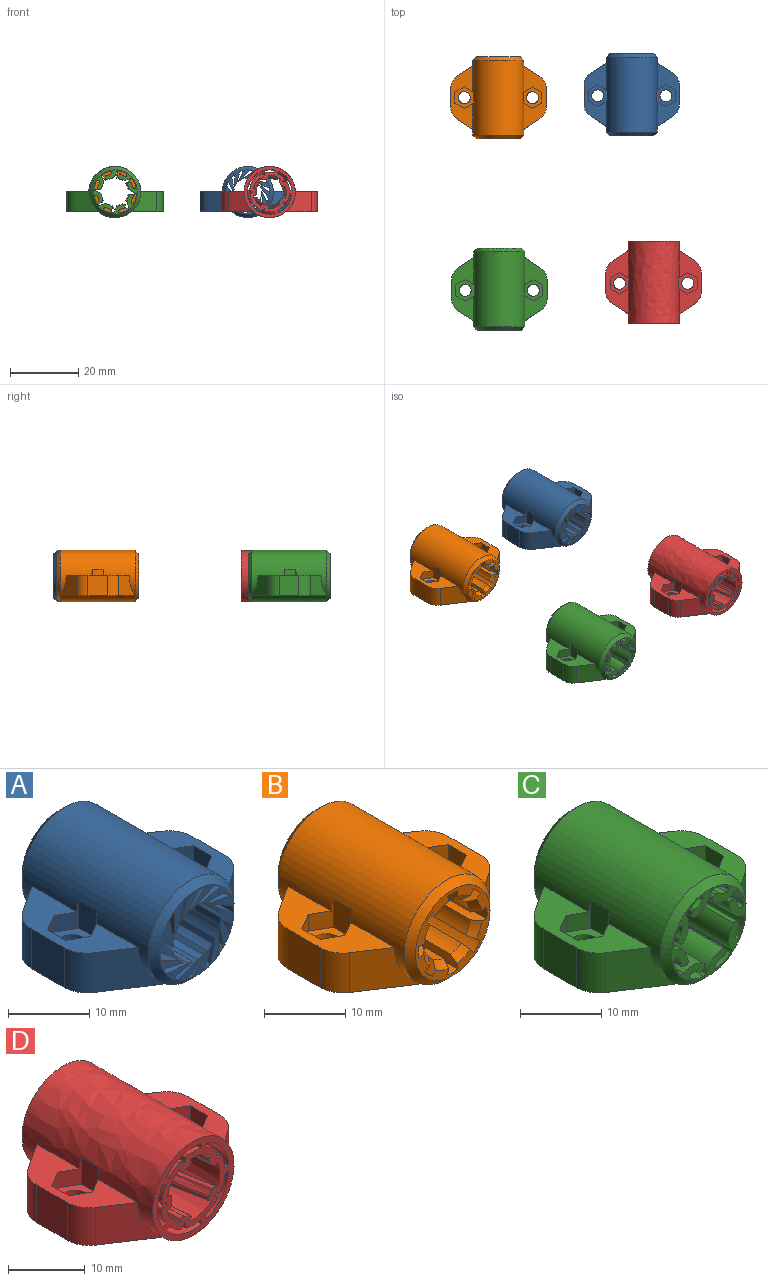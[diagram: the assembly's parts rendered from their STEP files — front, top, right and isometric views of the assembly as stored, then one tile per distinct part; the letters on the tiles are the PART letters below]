
ASSEMBLY  parts=4 mates=3
PART A: 96 faces, bbox 28x24x15 mm
  f0: plane 18.57x6.5mm, normal (0,0,1), area 66.1mm2, adj f1,f2,f6,f7,f8,f9,f87,f88
  f1: cylinder r=7.5mm len=22mm, axis (0,1,0), area 529.7mm2, adj f0,f6,f7,f69,f70,f71,f76,f77
  f2: plane 6x5.69mm, normal (-1,0,0), area 34.2mm2, adj f0,f3,f8,f9
  f3: plane 22x9.3mm, normal (0,0,-1), area 139mm2, adj f2,f4,f5,f6,f7,f8,f9,f10
  f4: plane 0.2x0.17mm, normal (0,-1,0), area 0mm2, adj f3,f6,f69
  f5: plane 0.2x0.17mm, normal (0,1,0), area 0mm2, adj f3,f7,f70
  f6: plane 7.3x6mm, normal (-0.55,-0.83,0), area 39.7mm2, adj f0,f1,f3,f4,f8
  f7: plane 7.3x6mm, normal (-0.55,0.83,0), area 39.7mm2, adj f0,f1,f3,f5,f9
  f8: cylinder r=4mm len=6mm, axis (0,0,-1), area 23.7mm2, adj f0,f2,f3,f6
  f9: cylinder r=4mm len=6mm, axis (0,0,-1), area 23.7mm2, adj f0,f2,f3,f7
  f10: cylinder r=7.5mm len=22mm, axis (0,1,0), area 223.5mm2, adj f3,f69,f70,f72
  f11: cylinder r=6.35mm len=24mm, axis (0,1,0), area 28.5mm2, adj f12,f66,f67,f68
  f12: plane 24x3.15mm, normal (-0.9,0,-0.44), area 84.3mm2, adj f11,f13,f67,f68
  f13: cylinder r=4.1mm len=24mm, axis (0,1,0), area 25.8mm2, adj f12,f14,f67,f68
  f14: plane 24x3.44mm, normal (0.98,0,0.2), area 84.3mm2, adj f13,f15,f67,f68
  f15: cylinder r=6.35mm len=24mm, axis (0,1,0), area 28.5mm2, adj f14,f16,f67,f68
  f16: plane 24x3.51mm, normal (-1,0,-0.01), area 84.3mm2, adj f15,f17,f67,f68
  f17: cylinder r=4.1mm len=24mm, axis (0,1,0), area 25.8mm2, adj f16,f18,f67,f68
  f18: plane 24x3.4mm, normal (0.97,0,-0.25), area 84.3mm2, adj f17,f19,f67,f68
  f19: cylinder r=6.35mm len=24mm, axis (0,1,0), area 28.5mm2, adj f18,f20,f67,f68
  f20: plane 24x3.18mm, normal (-0.91,0,0.42), area 84.3mm2, adj f19,f21,f67,f68
  f21: cylinder r=4.1mm len=24mm, axis (0,1,0), area 25.8mm2, adj f20,f22,f67,f68
  f22: plane 24x2.69mm, normal (0.77,0,-0.64), area 84.3mm2, adj f21,f23,f67,f68
  f23: cylinder r=6.35mm len=24mm, axis (0,1,0), area 28.5mm2, adj f22,f24,f67,f68
  f24: plane 24x2.72mm, normal (-0.63,0,0.77), area 84.3mm2, adj f23,f25,f67,f68
  f25: cylinder r=4.1mm len=24mm, axis (0,1,0), area 25.8mm2, adj f24,f26,f67,f68
  f26: plane 24x3.2mm, normal (0.41,0,-0.91), area 84.3mm2, adj f25,f27,f67,f68
  f27: cylinder r=6.35mm len=24mm, axis (0,1,0), area 28.5mm2, adj f26,f28,f67,f68
  f28: plane 24x3.42mm, normal (-0.23,0,0.97), area 84.3mm2, adj f27,f29,f67,f68
  f29: cylinder r=4.1mm len=24mm, axis (0,1,0), area 25.8mm2, adj f28,f30,f67,f68
  f30: plane 24x3.51mm, normal (-0.03,0,-1), area 84.3mm2, adj f29,f31,f67,f68
  f31: cylinder r=6.35mm len=24mm, axis (0,1,0), area 28.5mm2, adj f30,f32,f67,f68
  f32: plane 24x3.43mm, normal (0.21,0,0.98), area 84.3mm2, adj f31,f33,f67,f68
  f33: cylinder r=4.1mm len=24mm, axis (0,1,0), area 25.8mm2, adj f32,f34,f67,f68
  f34: plane 24x3.13mm, normal (-0.46,0,-0.89), area 84.3mm2, adj f33,f35,f67,f68
  f35: cylinder r=6.35mm len=24mm, axis (0,1,0), area 28.5mm2, adj f34,f36,f67,f68
  f36: plane 24x2.77mm, normal (0.61,0,0.79), area 84.3mm2, adj f35,f37,f67,f68
  f37: cylinder r=4.1mm len=24mm, axis (0,1,0), area 25.8mm2, adj f36,f38,f67,f68
  f38: plane 24x2.8mm, normal (-0.8,0,-0.6), area 84.3mm2, adj f37,f39,f67,f68
  f39: cylinder r=6.35mm len=24mm, axis (0,1,0), area 28.5mm2, adj f38,f40,f67,f68
  f40: plane 24x3.15mm, normal (0.9,0,0.44), area 84.3mm2, adj f39,f41,f67,f68
  f41: cylinder r=4.1mm len=24mm, axis (0,1,0), area 25.8mm2, adj f40,f42,f67,f68
  f42: plane 24x3.44mm, normal (-0.98,0,-0.2), area 84.3mm2, adj f41,f43,f67,f68
  f43: cylinder r=6.35mm len=24mm, axis (0,1,0), area 28.5mm2, adj f42,f44,f67,f68
  f44: plane 24x3.51mm, normal (1,0,0.01), area 84.3mm2, adj f43,f45,f67,f68
  f45: cylinder r=4.1mm len=24mm, axis (0,1,0), area 25.8mm2, adj f44,f46,f67,f68
  f46: plane 24x3.4mm, normal (-0.97,0,0.25), area 84.3mm2, adj f45,f47,f67,f68
  f47: cylinder r=6.35mm len=24mm, axis (0,1,0), area 28.5mm2, adj f46,f48,f67,f68
  f48: plane 24x3.18mm, normal (0.91,0,-0.42), area 84.3mm2, adj f47,f49,f67,f68
  f49: cylinder r=4.1mm len=24mm, axis (0,1,0), area 25.8mm2, adj f48,f50,f67,f68
  f50: plane 24x2.69mm, normal (-0.77,0,0.64), area 84.3mm2, adj f49,f51,f67,f68
  f51: cylinder r=6.35mm len=24mm, axis (0,1,0), area 28.5mm2, adj f50,f52,f67,f68
  f52: plane 24x2.72mm, normal (0.63,0,-0.77), area 84.3mm2, adj f51,f53,f67,f68
  f53: cylinder r=4.1mm len=24mm, axis (0,1,0), area 25.8mm2, adj f52,f54,f67,f68
  f54: plane 24x3.2mm, normal (-0.41,0,0.91), area 84.3mm2, adj f53,f55,f67,f68
  f55: cylinder r=6.35mm len=24mm, axis (0,1,0), area 28.5mm2, adj f54,f56,f67,f68
  f56: plane 24x3.42mm, normal (0.23,0,-0.97), area 84.3mm2, adj f55,f57,f67,f68
  f57: cylinder r=4.1mm len=24mm, axis (0,1,0), area 25.8mm2, adj f56,f58,f67,f68
  f58: plane 24x3.51mm, normal (0.03,0,1), area 84.3mm2, adj f57,f59,f67,f68
  f59: cylinder r=6.35mm len=24mm, axis (0,1,0), area 28.5mm2, adj f58,f60,f67,f68
  f60: plane 24x3.43mm, normal (-0.21,0,-0.98), area 84.3mm2, adj f59,f61,f67,f68
  f61: cylinder r=4.1mm len=24mm, axis (0,1,0), area 25.8mm2, adj f60,f62,f67,f68
  f62: plane 24x3.13mm, normal (0.46,0,0.89), area 84.3mm2, adj f61,f63,f67,f68
  f63: cylinder r=6.35mm len=24mm, axis (0,1,0), area 28.5mm2, adj f62,f64,f67,f68
  f64: plane 24x2.77mm, normal (-0.61,0,-0.79), area 84.3mm2, adj f63,f65,f67,f68
  f65: cylinder r=4.1mm len=24mm, axis (0,1,0), area 25.8mm2, adj f64,f66,f67,f68
  f66: plane 24x2.8mm, normal (0.8,0,0.6), area 84.3mm2, adj f11,f65,f67,f68
  f67: plane 13x13mm, normal (0,-1,0), area 49.1mm2, adj f11,f12,f13,f14,f15,f16,f17,f18
  f68: plane 13x13mm, normal (0,1,0), area 49.1mm2, adj f11,f12,f13,f14,f15,f16,f17,f18
  f69: cone r=6.5mm half-angle=45deg, axis (0,1,0), area 62.2mm2, adj f1,f4,f10,f67,f74
  f70: cone r=7.5mm half-angle=45deg, axis (0,-1,0), area 62.2mm2, adj f1,f5,f10,f68,f75
  f71: plane 18.57x6.5mm, normal (0,0,1), area 66.1mm2, adj f1,f73,f76,f77,f78,f79,f81,f82
  f72: plane 22x9.3mm, normal (0,0,-1), area 139mm2, adj f10,f73,f74,f75,f76,f77,f78,f79
  f73: plane 6x5.69mm, normal (1,0,0), area 34.2mm2, adj f71,f72,f78,f79
  f74: plane 0.2x0.17mm, normal (0,-1,0), area 0mm2, adj f69,f72,f77
  f75: plane 0.2x0.17mm, normal (0,1,0), area 0mm2, adj f70,f72,f76
  f76: plane 7.3x6mm, normal (0.55,0.83,0), area 39.7mm2, adj f1,f71,f72,f75,f78
  f77: plane 7.3x6mm, normal (0.55,-0.83,0), area 39.7mm2, adj f1,f71,f72,f74,f79
  f78: cylinder r=4mm len=6mm, axis (0,0,1), area 23.7mm2, adj f71,f72,f73,f76
  f79: cylinder r=4mm len=6mm, axis (0,0,1), area 23.7mm2, adj f71,f72,f73,f77
  f80: plane 4.3x3.18mm, normal (1,-0.01,0), area 13.5mm2, adj f1,f81,f82,f86
  f81: plane 4.3x2.74mm, normal (0.5,0.86,0), area 8.3mm2, adj f1,f71,f80,f83,f86
  f82: plane 4.23x2.76mm, normal (0.5,-0.87,0), area 8.2mm2, adj f1,f71,f80,f85,f86
  f83: plane 2.76x2.5mm, normal (-0.5,0.87,0), area 7.9mm2, adj f71,f81,f84,f86
  f84: plane 3.18x2.5mm, normal (-1,0.01,0), area 7.9mm2, adj f71,f83,f85,f86
  f85: plane 2.74x2.5mm, normal (-0.5,-0.86,0), area 7.9mm2, adj f71,f82,f84,f86
  f86: plane 6.35x5.52mm, normal (0,0,1), area 16.6mm2, adj f80,f81,f82,f83,f84,f85,f95
  f87: plane 2.74x2.5mm, normal (0.5,-0.86,0), area 7.9mm2, adj f0,f88,f92,f93
  f88: plane 3.18x2.5mm, normal (1,0.01,0), area 7.9mm2, adj f0,f87,f89,f93
  f89: plane 2.76x2.5mm, normal (0.5,0.87,0), area 7.9mm2, adj f0,f88,f90,f93
  f90: plane 4.3x2.74mm, normal (-0.5,0.86,0), area 8.3mm2, adj f0,f1,f89,f91,f93
  f91: plane 4.3x3.18mm, normal (-1,-0.01,0), area 13.5mm2, adj f1,f90,f92,f93
  f92: plane 4.23x2.76mm, normal (-0.5,-0.87,0), area 8.2mm2, adj f0,f1,f87,f91,f93
  f93: plane 6.35x5.52mm, normal (0,0,1), area 16.6mm2, adj f87,f88,f89,f90,f91,f92,f94
  f94: cylinder r=1.75mm len=3.5mm, axis (0,0,1), area 38.5mm2, adj f3,f93
  f95: cylinder r=1.75mm len=3.5mm, axis (0,0,1), area 38.5mm2, adj f72,f86
PART B: 88 faces, bbox 28x24x15 mm
  f0: plane 18.57x6.5mm, normal (0,0,1), area 66.1mm2, adj f1,f2,f6,f7,f8,f9,f79,f80
  f1: cylinder r=7.5mm len=22mm, axis (0,1,0), area 529.7mm2, adj f0,f6,f7,f45,f46,f63,f68,f69
  f2: plane 6x5.69mm, normal (-1,0,0), area 34.2mm2, adj f0,f3,f8,f9
  f3: plane 22x9.3mm, normal (0,0,-1), area 139mm2, adj f2,f4,f5,f6,f7,f8,f9,f10
  f4: plane 0.2x0.17mm, normal (0,-1,0), area 0mm2, adj f3,f6,f45
  f5: plane 0.2x0.17mm, normal (0,1,0), area 0mm2, adj f3,f7,f46
  f6: plane 7.3x6mm, normal (-0.55,-0.83,0), area 39.7mm2, adj f0,f1,f3,f4,f8
  f7: plane 7.3x6mm, normal (-0.55,0.83,0), area 39.7mm2, adj f0,f1,f3,f5,f9
  f8: cylinder r=4mm len=6mm, axis (0,0,-1), area 23.7mm2, adj f0,f2,f3,f6
  f9: cylinder r=4mm len=6mm, axis (0,0,-1), area 23.7mm2, adj f0,f2,f3,f7
  f10: cylinder r=7.5mm len=22mm, axis (0,1,0), area 223.5mm2, adj f3,f45,f46,f64
  f11: plane 24x1.54mm, normal (0.59,0,0.81), area 44.6mm2, adj f12,f42,f43,f44,f49,f61
  f12: cylinder r=6mm len=24mm, axis (0,1,0), area 42.5mm2, adj f11,f13,f43,f44
  f13: plane 24x1.54mm, normal (-0.81,0,-0.59), area 44.6mm2, adj f12,f14,f43,f44,f50,f62
  f14: cylinder r=4.1mm len=22mm, axis (0,1,0), area 44.9mm2, adj f13,f15,f50,f62
  f15: plane 24x1.88mm, normal (0.99,0,0.15), area 44.6mm2, adj f14,f16,f43,f44,f50,f62
  f16: cylinder r=6mm len=24mm, axis (0,1,0), area 42.5mm2, adj f15,f17,f43,f44
  f17: plane 24x1.88mm, normal (-0.99,0,0.15), area 44.6mm2, adj f16,f18,f43,f44,f51,f55
  f18: cylinder r=4.1mm len=22mm, axis (0,1,0), area 44.9mm2, adj f17,f19,f51,f55
  f19: plane 24x1.54mm, normal (0.81,0,-0.59), area 44.6mm2, adj f18,f20,f43,f44,f51,f55
  f20: cylinder r=6mm len=24mm, axis (0,1,0), area 42.5mm2, adj f19,f21,f43,f44
  f21: plane 24x1.54mm, normal (-0.59,0,0.81), area 44.6mm2, adj f20,f22,f43,f44,f52,f56
  f22: cylinder r=4.1mm len=22mm, axis (0,1,0), area 44.9mm2, adj f21,f23,f52,f56
  f23: plane 24x1.88mm, normal (0.15,0,-0.99), area 44.6mm2, adj f22,f24,f43,f44,f52,f56
  f24: cylinder r=6mm len=24mm, axis (0,1,0), area 42.5mm2, adj f23,f25,f43,f44
  f25: plane 24x1.88mm, normal (0.15,0,0.99), area 44.6mm2, adj f24,f26,f43,f44,f53,f57
  f26: cylinder r=4.1mm len=22mm, axis (0,1,0), area 44.9mm2, adj f25,f27,f53,f57
  f27: plane 24x1.54mm, normal (-0.59,0,-0.81), area 44.6mm2, adj f26,f28,f43,f44,f53,f57
  f28: cylinder r=6mm len=24mm, axis (0,1,0), area 42.5mm2, adj f27,f29,f43,f44
  f29: plane 24x1.54mm, normal (0.81,0,0.59), area 44.6mm2, adj f28,f30,f43,f44,f54,f58
  f30: cylinder r=4.1mm len=22mm, axis (0,1,0), area 44.9mm2, adj f29,f31,f54,f58
  f31: plane 24x1.88mm, normal (-0.99,0,-0.15), area 44.6mm2, adj f30,f32,f43,f44,f54,f58
  f32: cylinder r=6mm len=24mm, axis (0,1,0), area 42.5mm2, adj f31,f33,f43,f44
  f33: plane 24x1.88mm, normal (0.99,0,-0.15), area 44.6mm2, adj f32,f34,f43,f44,f47,f59
  f34: cylinder r=4.1mm len=22mm, axis (0,1,0), area 44.9mm2, adj f33,f35,f47,f59
  f35: plane 24x1.54mm, normal (-0.81,0,0.59), area 44.6mm2, adj f34,f36,f43,f44,f47,f59
  f36: cylinder r=6mm len=24mm, axis (0,1,0), area 42.5mm2, adj f35,f37,f43,f44
  f37: plane 24x1.54mm, normal (0.59,0,-0.81), area 44.6mm2, adj f36,f38,f43,f44,f48,f60
  f38: cylinder r=4.1mm len=22mm, axis (0,1,0), area 44.9mm2, adj f37,f39,f48,f60
  f39: plane 24x1.88mm, normal (-0.15,0,0.99), area 44.6mm2, adj f38,f40,f43,f44,f48,f60
  f40: cylinder r=6mm len=24mm, axis (0,1,0), area 42.5mm2, adj f39,f41,f43,f44
  f41: plane 24x1.88mm, normal (-0.15,0,-0.99), area 44.6mm2, adj f40,f42,f43,f44,f49,f61
  f42: cylinder r=4.1mm len=22mm, axis (0,1,0), area 44.9mm2, adj f11,f41,f49,f61
  f43: plane 13x13mm, normal (0,-1,0), area 39.3mm2, adj f11,f12,f13,f15,f16,f17,f19,f20
  f44: plane 13x13mm, normal (0,1,0), area 39.3mm2, adj f11,f12,f13,f15,f16,f17,f19,f20
  f45: cone r=6.5mm half-angle=45deg, axis (0,1,0), area 62.2mm2, adj f1,f4,f10,f43,f66
  f46: cone r=7.5mm half-angle=45deg, axis (0,-1,0), area 62.2mm2, adj f1,f5,f10,f44,f67
  f47: cone r=5.1mm half-angle=45deg, axis (0,1,0), area 3.2mm2, adj f33,f34,f35,f44
  f48: cone r=5.1mm half-angle=45deg, axis (0,1,0), area 3.2mm2, adj f37,f38,f39,f44
  f49: cone r=5.1mm half-angle=45deg, axis (0,1,0), area 3.2mm2, adj f11,f41,f42,f44
  f50: cone r=5.1mm half-angle=45deg, axis (0,1,0), area 3.2mm2, adj f13,f14,f15,f44
  f51: cone r=5.1mm half-angle=45deg, axis (0,1,0), area 3.2mm2, adj f17,f18,f19,f44
  f52: cone r=5.1mm half-angle=45deg, axis (0,1,0), area 3.2mm2, adj f21,f22,f23,f44
  f53: cone r=5.1mm half-angle=45deg, axis (0,1,0), area 3.2mm2, adj f25,f26,f27,f44
  f54: cone r=5.1mm half-angle=45deg, axis (0,1,0), area 3.2mm2, adj f29,f30,f31,f44
  f55: cone r=4.1mm half-angle=45deg, axis (0,-1,0), area 3.2mm2, adj f17,f18,f19,f43
  f56: cone r=4.1mm half-angle=45deg, axis (0,-1,0), area 3.2mm2, adj f21,f22,f23,f43
  f57: cone r=4.1mm half-angle=45deg, axis (0,-1,0), area 3.2mm2, adj f25,f26,f27,f43
  f58: cone r=4.1mm half-angle=45deg, axis (0,-1,0), area 3.2mm2, adj f29,f30,f31,f43
  f59: cone r=4.1mm half-angle=45deg, axis (0,-1,0), area 3.2mm2, adj f33,f34,f35,f43
  f60: cone r=4.1mm half-angle=45deg, axis (0,-1,0), area 3.2mm2, adj f37,f38,f39,f43
  f61: cone r=4.1mm half-angle=45deg, axis (0,-1,0), area 3.2mm2, adj f11,f41,f42,f43
  f62: cone r=4.1mm half-angle=45deg, axis (0,-1,0), area 3.2mm2, adj f13,f14,f15,f43
  f63: plane 18.57x6.5mm, normal (0,0,1), area 66.1mm2, adj f1,f65,f68,f69,f70,f71,f73,f74
  f64: plane 22x9.3mm, normal (0,0,-1), area 139mm2, adj f10,f65,f66,f67,f68,f69,f70,f71
  f65: plane 6x5.69mm, normal (1,0,0), area 34.2mm2, adj f63,f64,f70,f71
  f66: plane 0.2x0.17mm, normal (0,-1,0), area 0mm2, adj f45,f64,f69
  f67: plane 0.2x0.17mm, normal (0,1,0), area 0mm2, adj f46,f64,f68
  f68: plane 7.3x6mm, normal (0.55,0.83,0), area 39.7mm2, adj f1,f63,f64,f67,f70
  f69: plane 7.3x6mm, normal (0.55,-0.83,0), area 39.7mm2, adj f1,f63,f64,f66,f71
  f70: cylinder r=4mm len=6mm, axis (0,0,1), area 23.7mm2, adj f63,f64,f65,f68
  f71: cylinder r=4mm len=6mm, axis (0,0,1), area 23.7mm2, adj f63,f64,f65,f69
  f72: plane 4.3x3.18mm, normal (1,-0.01,0), area 13.5mm2, adj f1,f73,f74,f78
  f73: plane 4.3x2.74mm, normal (0.5,0.86,0), area 8.3mm2, adj f1,f63,f72,f75,f78
  f74: plane 4.23x2.76mm, normal (0.5,-0.87,0), area 8.2mm2, adj f1,f63,f72,f77,f78
  f75: plane 2.76x2.5mm, normal (-0.5,0.87,0), area 7.9mm2, adj f63,f73,f76,f78
  f76: plane 3.18x2.5mm, normal (-1,0.01,0), area 7.9mm2, adj f63,f75,f77,f78
  f77: plane 2.74x2.5mm, normal (-0.5,-0.86,0), area 7.9mm2, adj f63,f74,f76,f78
  f78: plane 6.35x5.52mm, normal (0,0,1), area 16.6mm2, adj f72,f73,f74,f75,f76,f77,f87
  f79: plane 2.74x2.5mm, normal (0.5,-0.86,0), area 7.9mm2, adj f0,f80,f84,f85
  f80: plane 3.18x2.5mm, normal (1,0.01,0), area 7.9mm2, adj f0,f79,f81,f85
  f81: plane 2.76x2.5mm, normal (0.5,0.87,0), area 7.9mm2, adj f0,f80,f82,f85
  f82: plane 4.3x2.74mm, normal (-0.5,0.86,0), area 8.3mm2, adj f0,f1,f81,f83,f85
  f83: plane 4.3x3.18mm, normal (-1,-0.01,0), area 13.5mm2, adj f1,f82,f84,f85
  f84: plane 4.23x2.76mm, normal (-0.5,-0.87,0), area 8.2mm2, adj f0,f1,f79,f83,f85
  f85: plane 6.35x5.52mm, normal (0,0,1), area 16.6mm2, adj f79,f80,f81,f82,f83,f84,f86
  f86: cylinder r=1.75mm len=3.5mm, axis (0,0,1), area 38.5mm2, adj f3,f85
  f87: cylinder r=1.75mm len=3.5mm, axis (0,0,1), area 38.5mm2, adj f64,f78
PART C: 104 faces, bbox 28x24x15 mm
  f0: plane 18.57x6.5mm, normal (0,0,1), area 66.1mm2, adj f1,f2,f6,f7,f8,f9,f95,f96
  f1: cylinder r=7.5mm len=22mm, axis (0,1,0), area 529.7mm2, adj f0,f6,f7,f77,f78,f79,f84,f85
  f2: plane 6x5.69mm, normal (-1,0,0), area 34.2mm2, adj f0,f3,f8,f9
  f3: plane 22x9.3mm, normal (0,0,-1), area 139mm2, adj f2,f4,f5,f6,f7,f8,f9,f10
  f4: plane 0.2x0.17mm, normal (0,-1,0), area 0mm2, adj f3,f6,f77
  f5: plane 0.2x0.17mm, normal (0,1,0), area 0mm2, adj f3,f7,f78
  f6: plane 7.3x6mm, normal (-0.55,-0.83,0), area 39.7mm2, adj f0,f1,f3,f4,f8
  f7: plane 7.3x6mm, normal (-0.55,0.83,0), area 39.7mm2, adj f0,f1,f3,f5,f9
  f8: cylinder r=4mm len=6mm, axis (0,0,-1), area 23.7mm2, adj f0,f2,f3,f6
  f9: cylinder r=4mm len=6mm, axis (0,0,-1), area 23.7mm2, adj f0,f2,f3,f7
  f10: cylinder r=7.5mm len=22mm, axis (0,1,0), area 223.5mm2, adj f3,f77,f78,f80
  f11: cylinder r=6.26mm len=24mm, axis (0,1,0), area 61.4mm2, adj f12,f74,f75,f76
  f12: cylinder r=0.4mm len=24mm, axis (0,1,0), area 24.8mm2, adj f11,f13,f75,f76
  f13: cylinder r=1.94mm len=24mm, axis (0,1,0), area 36.8mm2, adj f12,f14,f75,f76
  f14: cylinder r=0.4mm len=24mm, axis (0,1,0), area 13.3mm2, adj f13,f15,f75,f76
  f15: plane 24x0.35mm, normal (-0.58,0,0.82), area 10.3mm2, adj f14,f16,f75,f76
  f16: cylinder r=0.4mm len=24mm, axis (0,1,0), area 17.1mm2, adj f15,f17,f75,f76
  f17: cylinder r=3.19mm len=24mm, axis (0,1,0), area 96.2mm2, adj f16,f18,f75,f76
  f18: cylinder r=0.4mm len=24mm, axis (0,1,0), area 13.7mm2, adj f17,f19,f75,f76
  f19: cylinder r=6.26mm len=24mm, axis (0,1,0), area 61.4mm2, adj f18,f20,f75,f76
  f20: cylinder r=0.4mm len=24mm, axis (0,1,0), area 24.8mm2, adj f19,f21,f75,f76
  f21: cylinder r=1.94mm len=24mm, axis (0,1,0), area 36.8mm2, adj f20,f22,f75,f76
  f22: cylinder r=0.4mm len=24mm, axis (0,1,0), area 13.3mm2, adj f21,f23,f75,f76
  f23: plane 24x0.42mm, normal (0.17,0,0.99), area 10.3mm2, adj f22,f24,f75,f76
  f24: cylinder r=0.4mm len=24mm, axis (0,1,0), area 17.1mm2, adj f23,f25,f75,f76
  f25: cylinder r=3.19mm len=24mm, axis (0,1,0), area 96.2mm2, adj f24,f26,f75,f76
  f26: cylinder r=0.4mm len=24mm, axis (0,1,0), area 13.7mm2, adj f25,f27,f75,f76
  f27: cylinder r=6.26mm len=24mm, axis (0,1,0), area 61.4mm2, adj f26,f28,f75,f76
  f28: cylinder r=0.4mm len=24mm, axis (0,1,0), area 24.8mm2, adj f27,f29,f75,f76
  f29: cylinder r=1.94mm len=24mm, axis (0,1,0), area 36.8mm2, adj f28,f30,f75,f76
  f30: cylinder r=0.4mm len=24mm, axis (0,1,0), area 13.3mm2, adj f29,f31,f75,f76
  f31: plane 24x0.35mm, normal (0.82,0,0.58), area 10.3mm2, adj f30,f32,f75,f76
  f32: cylinder r=0.4mm len=24mm, axis (0,1,0), area 17.1mm2, adj f31,f33,f75,f76
  f33: cylinder r=3.19mm len=24mm, axis (0,1,0), area 96.2mm2, adj f32,f34,f75,f76
  f34: cylinder r=0.4mm len=24mm, axis (0,1,0), area 13.7mm2, adj f33,f35,f75,f76
  f35: cylinder r=6.26mm len=24mm, axis (0,1,0), area 61.4mm2, adj f34,f36,f75,f76
  f36: cylinder r=0.4mm len=24mm, axis (0,1,0), area 24.8mm2, adj f35,f37,f75,f76
  f37: cylinder r=1.94mm len=24mm, axis (0,1,0), area 36.8mm2, adj f36,f38,f75,f76
  f38: cylinder r=0.4mm len=24mm, axis (0,1,0), area 13.3mm2, adj f37,f39,f75,f76
  f39: plane 24x0.42mm, normal (0.99,0,-0.17), area 10.3mm2, adj f38,f40,f75,f76
  f40: cylinder r=0.4mm len=24mm, axis (0,1,0), area 17.1mm2, adj f39,f41,f75,f76
  f41: cylinder r=3.19mm len=24mm, axis (0,1,0), area 96.2mm2, adj f40,f42,f75,f76
  f42: cylinder r=0.4mm len=24mm, axis (0,1,0), area 13.7mm2, adj f41,f43,f75,f76
  f43: cylinder r=6.26mm len=24mm, axis (0,1,0), area 61.4mm2, adj f42,f44,f75,f76
  f44: cylinder r=0.4mm len=24mm, axis (0,1,0), area 24.8mm2, adj f43,f45,f75,f76
  f45: cylinder r=1.94mm len=24mm, axis (0,1,0), area 36.8mm2, adj f44,f46,f75,f76
  f46: cylinder r=0.4mm len=24mm, axis (0,1,0), area 13.3mm2, adj f45,f47,f75,f76
  f47: plane 24x0.35mm, normal (0.58,0,-0.82), area 10.3mm2, adj f46,f48,f75,f76
  f48: cylinder r=0.4mm len=24mm, axis (0,1,0), area 17.1mm2, adj f47,f49,f75,f76
  f49: cylinder r=3.19mm len=24mm, axis (0,1,0), area 96.2mm2, adj f48,f50,f75,f76
  f50: cylinder r=0.4mm len=24mm, axis (0,1,0), area 13.7mm2, adj f49,f51,f75,f76
  f51: cylinder r=6.26mm len=24mm, axis (0,1,0), area 61.4mm2, adj f50,f52,f75,f76
  f52: cylinder r=0.4mm len=24mm, axis (0,1,0), area 24.8mm2, adj f51,f53,f75,f76
  f53: cylinder r=1.94mm len=24mm, axis (0,1,0), area 36.8mm2, adj f52,f54,f75,f76
  f54: cylinder r=0.4mm len=24mm, axis (0,1,0), area 13.3mm2, adj f53,f55,f75,f76
  f55: plane 24x0.42mm, normal (-0.17,0,-0.99), area 10.3mm2, adj f54,f56,f75,f76
  f56: cylinder r=0.4mm len=24mm, axis (0,1,0), area 17.1mm2, adj f55,f57,f75,f76
  f57: cylinder r=3.19mm len=24mm, axis (0,1,0), area 96.2mm2, adj f56,f58,f75,f76
  f58: cylinder r=0.4mm len=24mm, axis (0,1,0), area 13.7mm2, adj f57,f59,f75,f76
  f59: cylinder r=6.26mm len=24mm, axis (0,1,0), area 61.4mm2, adj f58,f60,f75,f76
  f60: cylinder r=0.4mm len=24mm, axis (0,1,0), area 24.8mm2, adj f59,f61,f75,f76
  f61: cylinder r=1.94mm len=24mm, axis (0,1,0), area 36.8mm2, adj f60,f62,f75,f76
  f62: cylinder r=0.4mm len=24mm, axis (0,1,0), area 13.3mm2, adj f61,f63,f75,f76
  f63: plane 24x0.35mm, normal (-0.82,0,-0.58), area 10.3mm2, adj f62,f64,f75,f76
  f64: cylinder r=0.4mm len=24mm, axis (0,1,0), area 17.1mm2, adj f63,f65,f75,f76
  f65: cylinder r=3.19mm len=24mm, axis (0,1,0), area 96.2mm2, adj f64,f66,f75,f76
  f66: cylinder r=0.4mm len=24mm, axis (0,1,0), area 13.7mm2, adj f65,f67,f75,f76
  f67: cylinder r=6.26mm len=24mm, axis (0,1,0), area 61.4mm2, adj f66,f68,f75,f76
  f68: cylinder r=0.4mm len=24mm, axis (0,1,0), area 24.8mm2, adj f67,f69,f75,f76
  f69: cylinder r=1.94mm len=24mm, axis (0,1,0), area 36.8mm2, adj f68,f70,f75,f76
  f70: cylinder r=0.4mm len=24mm, axis (0,1,0), area 13.3mm2, adj f69,f71,f75,f76
  f71: plane 24x0.42mm, normal (-0.99,0,0.17), area 10.3mm2, adj f70,f72,f75,f76
  f72: cylinder r=0.4mm len=24mm, axis (0,1,0), area 17.1mm2, adj f71,f73,f75,f76
  f73: cylinder r=3.19mm len=24mm, axis (0,1,0), area 96.2mm2, adj f72,f74,f75,f76
  f74: cylinder r=0.4mm len=24mm, axis (0,1,0), area 13.7mm2, adj f11,f73,f75,f76
  f75: plane 13x13mm, normal (0,-1,0), area 46.1mm2, adj f11,f12,f13,f14,f15,f16,f17,f18
  f76: plane 13x13mm, normal (0,1,0), area 46.1mm2, adj f11,f12,f13,f14,f15,f16,f17,f18
  f77: cone r=6.5mm half-angle=45deg, axis (0,1,0), area 62.2mm2, adj f1,f4,f10,f75,f82
  f78: cone r=7.5mm half-angle=45deg, axis (0,-1,0), area 62.2mm2, adj f1,f5,f10,f76,f83
  f79: plane 18.57x6.5mm, normal (0,0,1), area 66.1mm2, adj f1,f81,f84,f85,f86,f87,f89,f90
  f80: plane 22x9.3mm, normal (0,0,-1), area 139mm2, adj f10,f81,f82,f83,f84,f85,f86,f87
  f81: plane 6x5.69mm, normal (1,0,0), area 34.2mm2, adj f79,f80,f86,f87
  f82: plane 0.2x0.17mm, normal (0,-1,0), area 0mm2, adj f77,f80,f85
  f83: plane 0.2x0.17mm, normal (0,1,0), area 0mm2, adj f78,f80,f84
  f84: plane 7.3x6mm, normal (0.55,0.83,0), area 39.7mm2, adj f1,f79,f80,f83,f86
  f85: plane 7.3x6mm, normal (0.55,-0.83,0), area 39.7mm2, adj f1,f79,f80,f82,f87
  f86: cylinder r=4mm len=6mm, axis (0,0,1), area 23.7mm2, adj f79,f80,f81,f84
  f87: cylinder r=4mm len=6mm, axis (0,0,1), area 23.7mm2, adj f79,f80,f81,f85
  f88: plane 4.3x3.18mm, normal (1,-0.01,0), area 13.5mm2, adj f1,f89,f90,f94
  f89: plane 4.3x2.74mm, normal (0.5,0.86,0), area 8.3mm2, adj f1,f79,f88,f91,f94
  f90: plane 4.23x2.76mm, normal (0.5,-0.87,0), area 8.2mm2, adj f1,f79,f88,f93,f94
  f91: plane 2.76x2.5mm, normal (-0.5,0.87,0), area 7.9mm2, adj f79,f89,f92,f94
  f92: plane 3.18x2.5mm, normal (-1,0.01,0), area 7.9mm2, adj f79,f91,f93,f94
  f93: plane 2.74x2.5mm, normal (-0.5,-0.86,0), area 7.9mm2, adj f79,f90,f92,f94
  f94: plane 6.35x5.52mm, normal (0,0,1), area 16.6mm2, adj f88,f89,f90,f91,f92,f93,f103
  f95: plane 2.74x2.5mm, normal (0.5,-0.86,0), area 7.9mm2, adj f0,f96,f100,f101
  f96: plane 3.18x2.5mm, normal (1,0.01,0), area 7.9mm2, adj f0,f95,f97,f101
  f97: plane 2.76x2.5mm, normal (0.5,0.87,0), area 7.9mm2, adj f0,f96,f98,f101
  f98: plane 4.3x2.74mm, normal (-0.5,0.86,0), area 8.3mm2, adj f0,f1,f97,f99,f101
  f99: plane 4.3x3.18mm, normal (-1,-0.01,0), area 13.5mm2, adj f1,f98,f100,f101
  f100: plane 4.23x2.76mm, normal (-0.5,-0.87,0), area 8.2mm2, adj f0,f1,f95,f99,f101
  f101: plane 6.35x5.52mm, normal (0,0,1), area 16.6mm2, adj f95,f96,f97,f98,f99,f100,f102
  f102: cylinder r=1.75mm len=3.5mm, axis (0,0,1), area 38.5mm2, adj f3,f101
  f103: cylinder r=1.75mm len=3.5mm, axis (0,0,1), area 38.5mm2, adj f80,f94
PART D: 117 faces, bbox 28.1x32.8x15.1 mm
  f0: bspline ~24x15mm, area 847.8mm2, adj f1,f2,f3,f5,f6,f7,f8,f12
  f1: plane 18.57x6.5mm, normal (0,0,1), area 66.1mm2, adj f0,f11,f15,f16,f17,f18,f101,f102
  f2: plane 18.57x6.5mm, normal (0,0,1), area 66.1mm2, adj f0,f4,f7,f8,f9,f10,f108,f109
  f3: plane 22x9.3mm, normal (0,0,-1), area 139mm2, adj f0,f4,f5,f6,f7,f8,f9,f10
  f4: plane 6x5.69mm, normal (1,0,0), area 34.2mm2, adj f2,f3,f9,f10
  f5: plane 0.2x0.17mm, normal (0,-1,0), area 0mm2, adj f0,f3,f8
  f6: plane 0.2x0.17mm, normal (0,1,0), area 0mm2, adj f0,f3,f7
  f7: plane 7.3x6mm, normal (0.55,0.83,0), area 39.7mm2, adj f0,f2,f3,f6,f9
  f8: plane 7.3x6mm, normal (0.55,-0.83,0), area 39.7mm2, adj f0,f2,f3,f5,f10
  f9: cylinder r=4mm len=6mm, axis (0,0,1), area 23.7mm2, adj f2,f3,f4,f7
  f10: cylinder r=4mm len=6mm, axis (0,0,1), area 23.7mm2, adj f2,f3,f4,f8
  f11: plane 6x5.69mm, normal (-1,0,0), area 34.2mm2, adj f1,f12,f17,f18
  f12: plane 22x9.3mm, normal (0,0,-1), area 139mm2, adj f0,f11,f13,f14,f15,f16,f17,f18
  f13: plane 0.2x0.17mm, normal (0,-1,0), area 0mm2, adj f0,f12,f15
  f14: plane 0.2x0.17mm, normal (0,1,0), area 0mm2, adj f0,f12,f16
  f15: plane 7.3x6mm, normal (-0.55,-0.83,0), area 39.7mm2, adj f0,f1,f12,f13,f17
  f16: plane 7.3x6mm, normal (-0.55,0.83,0), area 39.7mm2, adj f0,f1,f12,f14,f18
  f17: cylinder r=4mm len=6mm, axis (0,0,-1), area 23.7mm2, adj f1,f11,f12,f15
  f18: cylinder r=4mm len=6mm, axis (0,0,-1), area 23.7mm2, adj f1,f11,f12,f16
  f19: bspline ~24x3.19mm, area 7.8mm2, adj f20,f28,f69,f70
  f20: bspline ~32.73x4.39mm, area 10.3mm2, adj f19,f21,f69,f70
  f21: bspline ~32.73x5.17mm, area 18.9mm2, adj f20,f22,f69,f70
  f22: bspline ~32.73x6.92mm, area 59.4mm2, adj f21,f23,f69,f70
  f23: bspline ~32.73x5.12mm, area 17.7mm2, adj f22,f24,f69,f70
  f24: bspline ~32.73x10.75mm, area 176.1mm2, adj f23,f25,f69,f70
  f25: bspline ~32.73x4.25mm, area 17.7mm2, adj f24,f26,f69,f70
  f26: bspline ~32.73x6mm, area 59.4mm2, adj f25,f27,f69,f70
  f27: bspline ~24x3.79mm, area 18.9mm2, adj f26,f28,f69,f70
  f28: bspline ~32.73x4.32mm, area 10.3mm2, adj f19,f27,f69,f70
  f29: bspline ~24x3.35mm, area 7.8mm2, adj f30,f38,f69,f70
  f30: bspline ~24x3.3mm, area 10.3mm2, adj f29,f31,f69,f70
  f31: bspline ~32.73x5.17mm, area 18.9mm2, adj f30,f32,f69,f70
  f32: bspline ~32.73x6.28mm, area 59.4mm2, adj f31,f33,f69,f70
  f33: bspline ~32.73x4.5mm, area 17.7mm2, adj f32,f34,f69,f70
  f34: bspline ~32.73x10.9mm, area 176.1mm2, adj f33,f35,f69,f70
  f35: bspline ~32.73x5mm, area 17.7mm2, adj f34,f36,f69,f70
  f36: bspline ~32.73x6.81mm, area 59.4mm2, adj f35,f37,f69,f70
  f37: bspline ~24x3.96mm, area 18.9mm2, adj f36,f38,f69,f70
  f38: bspline ~32.73x4.43mm, area 10.3mm2, adj f29,f37,f69,f70
  f39: bspline ~24x3.19mm, area 7.8mm2, adj f40,f48,f69,f70
  f40: bspline ~32.73x4.02mm, area 10.3mm2, adj f39,f41,f69,f70
  f41: bspline ~32.73x4.65mm, area 18.9mm2, adj f40,f42,f69,f70
  f42: bspline ~32.73x5.03mm, area 59.4mm2, adj f41,f43,f69,f70
  f43: bspline ~32.73x4.62mm, area 17.7mm2, adj f42,f44,f69,f70
  f44: bspline ~32.73x9.98mm, area 176.1mm2, adj f43,f45,f69,f70
  f45: bspline ~24x3.94mm, area 17.7mm2, adj f44,f46,f69,f70
  f46: bspline ~32.73x6.96mm, area 59.4mm2, adj f45,f47,f69,f70
  f47: bspline ~24x3.79mm, area 18.9mm2, adj f46,f48,f69,f70
  f48: bspline ~32.73x4.11mm, area 10.3mm2, adj f39,f47,f69,f70
  f49: bspline ~24x2.71mm, area 7.8mm2, adj f50,f58,f69,f70
  f50: bspline ~32.73x3.33mm, area 10.3mm2, adj f49,f51,f69,f70
  f51: bspline ~32.73x3.84mm, area 18.9mm2, adj f50,f52,f69,f70
  f52: bspline ~32.73x6.16mm, area 59.4mm2, adj f51,f53,f69,f70
  f53: bspline ~32.73x5.26mm, area 17.7mm2, adj f52,f54,f69,f70
  f54: bspline ~32.73x8.49mm, area 176.1mm2, adj f53,f55,f69,f70
  f55: bspline ~24x4.05mm, area 17.7mm2, adj f54,f56,f69,f70
  f56: bspline ~32.73x6.42mm, area 59.4mm2, adj f55,f57,f69,f70
  f57: bspline ~24x3.3mm, area 18.9mm2, adj f56,f58,f69,f70
  f58: bspline ~32.73x3.47mm, area 10.3mm2, adj f49,f57,f69,f70
  f59: bspline ~32.73x3.95mm, area 10.3mm2, adj f60,f68,f69,f70
  f60: bspline ~32.73x4.7mm, area 18.9mm2, adj f59,f61,f69,f70
  f61: bspline ~32.73x6.88mm, area 59.4mm2, adj f60,f62,f69,f70
  f62: bspline ~32.73x5.46mm, area 17.7mm2, adj f61,f63,f69,f70
  f63: bspline ~32.73x9.55mm, area 176.1mm2, adj f62,f64,f69,f70
  f64: bspline ~32.73x4.8mm, area 17.7mm2, adj f63,f65,f69,f70
  f65: bspline ~32.73x5.26mm, area 59.4mm2, adj f64,f66,f69,f70
  f66: bspline ~32.73x4.46mm, area 18.9mm2, adj f65,f67,f69,f70
  f67: bspline ~32.73x3.87mm, area 10.3mm2, adj f66,f68,f69,f70
  f68: bspline ~32.73x3.82mm, area 7.8mm2, adj f59,f67,f69,f70
  f69: plane 15.07x15.07mm, normal (0,1,0), area 82mm2, adj f0,f19,f20,f21,f22,f23,f24,f25
  f70: plane 15.1x15.1mm, normal (0,-1,0), area 82mm2, adj f0,f19,f20,f21,f22,f23,f24,f25
  f71: bspline ~32.73x6.66mm, area 96.9mm2, adj f69,f70,f72,f100
  f72: bspline ~32.73x4.09mm, area 10.7mm2, adj f69,f70,f71,f73
  f73: bspline ~24x2.94mm, area 17.5mm2, adj f69,f70,f72,f74
  f74: bspline ~32.73x4.12mm, area 23.8mm2, adj f69,f70,f73,f75
  f75: bspline ~32.73x3.8mm, area 17.5mm2, adj f69,f70,f74,f76
  f76: bspline ~32.73x3.74mm, area 10.7mm2, adj f69,f70,f75,f77
  f77: bspline ~32.73x5.41mm, area 96.9mm2, adj f69,f70,f76,f78
  f78: bspline ~32.73x3.87mm, area 10.7mm2, adj f69,f70,f77,f79
  f79: bspline ~32.73x3.88mm, area 17.5mm2, adj f69,f70,f78,f80
  f80: bspline ~32.73x4.17mm, area 23.8mm2, adj f69,f70,f79,f81
  f81: bspline ~32.73x3.94mm, area 17.5mm2, adj f69,f70,f80,f82
  f82: bspline ~32.73x4.07mm, area 10.7mm2, adj f69,f70,f81,f83
  f83: bspline ~32.73x6.38mm, area 96.9mm2, adj f69,f70,f82,f84
  f84: bspline ~32.73x3.32mm, area 10.7mm2, adj f69,f70,f83,f85
  f85: bspline ~32.73x3.47mm, area 17.5mm2, adj f69,f70,f84,f86
  f86: bspline ~32.73x3.82mm, area 23.8mm2, adj f69,f70,f85,f87
  f87: bspline ~32.73x3.69mm, area 17.5mm2, adj f69,f70,f86,f88
  f88: bspline ~24x3.03mm, area 10.7mm2, adj f69,f70,f87,f89
  f89: bspline ~32.73x7.18mm, area 96.9mm2, adj f69,f70,f88,f90
  f90: bspline ~32.73x3.47mm, area 10.7mm2, adj f69,f70,f89,f91
  f91: bspline ~32.73x3.15mm, area 17.5mm2, adj f69,f70,f90,f92
  f92: bspline ~32.73x3.09mm, area 23.8mm2, adj f69,f70,f91,f93
  f93: bspline ~32.73x3.29mm, area 17.5mm2, adj f69,f70,f92,f94
  f94: bspline ~32.73x3.63mm, area 10.7mm2, adj f69,f70,f93,f95
  f95: bspline ~32.73x7.28mm, area 96.9mm2, adj f69,f70,f94,f96
  f96: bspline ~24x2.88mm, area 10.7mm2, adj f69,f70,f95,f97
  f97: bspline ~32.73x3.57mm, area 17.5mm2, adj f69,f70,f96,f98
  f98: bspline ~32.73x3.66mm, area 23.8mm2, adj f69,f70,f97,f99
  f99: bspline ~32.73x3.3mm, area 17.5mm2, adj f69,f70,f98,f100
  f100: bspline ~32.73x3.14mm, area 10.7mm2, adj f69,f70,f71,f99
  f101: plane 2.74x2.5mm, normal (0.5,-0.86,0), area 7.9mm2, adj f1,f102,f106,f107
  f102: plane 3.18x2.5mm, normal (1,0.01,0), area 7.9mm2, adj f1,f101,f103,f107
  f103: plane 2.76x2.5mm, normal (0.5,0.87,0), area 7.9mm2, adj f1,f102,f104,f107
  f104: plane 4.3x2.74mm, normal (-0.5,0.86,0), area 8.3mm2, adj f0,f1,f103,f105,f107
  f105: plane 4.3x3.18mm, normal (-1,-0.01,0), area 13.5mm2, adj f0,f104,f106,f107
  f106: plane 4.23x2.76mm, normal (-0.5,-0.87,0), area 8.2mm2, adj f0,f1,f101,f105,f107
  f107: plane 6.35x5.52mm, normal (0,0,1), area 16.6mm2, adj f101,f102,f103,f104,f105,f106,f115
  f108: plane 4.3x2.74mm, normal (0.5,0.86,0), area 8.3mm2, adj f0,f2,f109,f113,f114
  f109: plane 2.76x2.5mm, normal (-0.5,0.87,0), area 7.9mm2, adj f2,f108,f110,f114
  f110: plane 3.18x2.5mm, normal (-1,0.01,0), area 7.9mm2, adj f2,f109,f111,f114
  f111: plane 2.74x2.5mm, normal (-0.5,-0.86,0), area 7.9mm2, adj f2,f110,f112,f114
  f112: plane 4.23x2.76mm, normal (0.5,-0.87,0), area 8.2mm2, adj f0,f2,f111,f113,f114
  f113: plane 4.3x3.18mm, normal (1,-0.01,0), area 13.5mm2, adj f0,f108,f112,f114
  f114: plane 6.35x5.52mm, normal (0,0,1), area 16.6mm2, adj f108,f109,f110,f111,f112,f113,f116
  f115: cylinder r=1.75mm len=3.5mm, axis (0,0,1), area 38.5mm2, adj f12,f107
  f116: cylinder r=1.75mm len=3.5mm, axis (0,0,1), area 38.5mm2, adj f3,f114
PLACE A t=(19.6,-18.27,-107.83)mm
PLACE B t=(-19.5,-19.15,-113.67)mm
PLACE C t=(-19.23,-75.3,-107.83)mm
PLACE D t=(26.01,-73.26,-107.83)mm
MATE planar C.f103 <-> D.f115  axis (0,0,-1) through (-9.23,-75.6,-113.67)mm
MATE planar B.f64 <-> A.f3  axis (0,0,-1) through (-10.94,-27.74,-113.67)mm
MATE planar B.f70 <-> C.f103  axis (0,0,-1) through (-9.5,-16.3,-113.67)mm
